FCSTD DOCUMENT  (FreeCAD 0.21R33771 (Git))
Label: Lidar
License: All rights reserved
LicenseURL: https://en.wikipedia.org/wiki/All_rights_reserved
objects: Sketcher::SketchObject×1
note: 1 computed .brp shape members not serialized (recipe doc carries the construction recipe); baked Part::Feature solids carry a one-line shape summary decoded from their .brp

FEATURE [Sketcher::SketchObject] Sketch
  FullyConstrained = false
  sketch-geometry (7):
    g0: LineSegment StartX=60 StartY=30 StartZ=0 EndX=45 EndY=55.9808 EndZ=0
    g1: LineSegment StartX=45 StartY=55.9808 StartZ=0 EndX=15 EndY=55.9808 EndZ=0
    g2: LineSegment StartX=15 StartY=55.9808 StartZ=0 EndX=-1.8e-15 EndY=30 EndZ=0
    g3: LineSegment StartX=0 StartY=30 StartZ=0 EndX=15 EndY=4.01924 EndZ=0
    g4: LineSegment StartX=15 StartY=4.01924 StartZ=0 EndX=45 EndY=4.01924 EndZ=0
    g5: LineSegment StartX=45 StartY=4.01924 StartZ=0 EndX=60 EndY=30 EndZ=0
    g6: Circle CenterX=30 CenterY=30 CenterZ=0 NormalX=0 NormalY=0 NormalZ=1 AngleXU=0 Radius=30
  constraints (13):
    c: Coincident(g0,g1)
    c: Coincident(g1,g2)
    c: Coincident(g2,g3)
    c: Coincident(g3,g4)
    c: Coincident(g4,g5)
    c: Coincident(g5,g0)
    c: Equal(g0, g1-g5) x5
    c: PointOnObject(g0,g6)
    c: PointOnObject(g1,g6)
    c: PointOnObject(g2,g6)
    c: PointOnObject(g3,g6)
    c: PointOnObject(g4,g6)
    c: PointOnObject(g5,g6)
